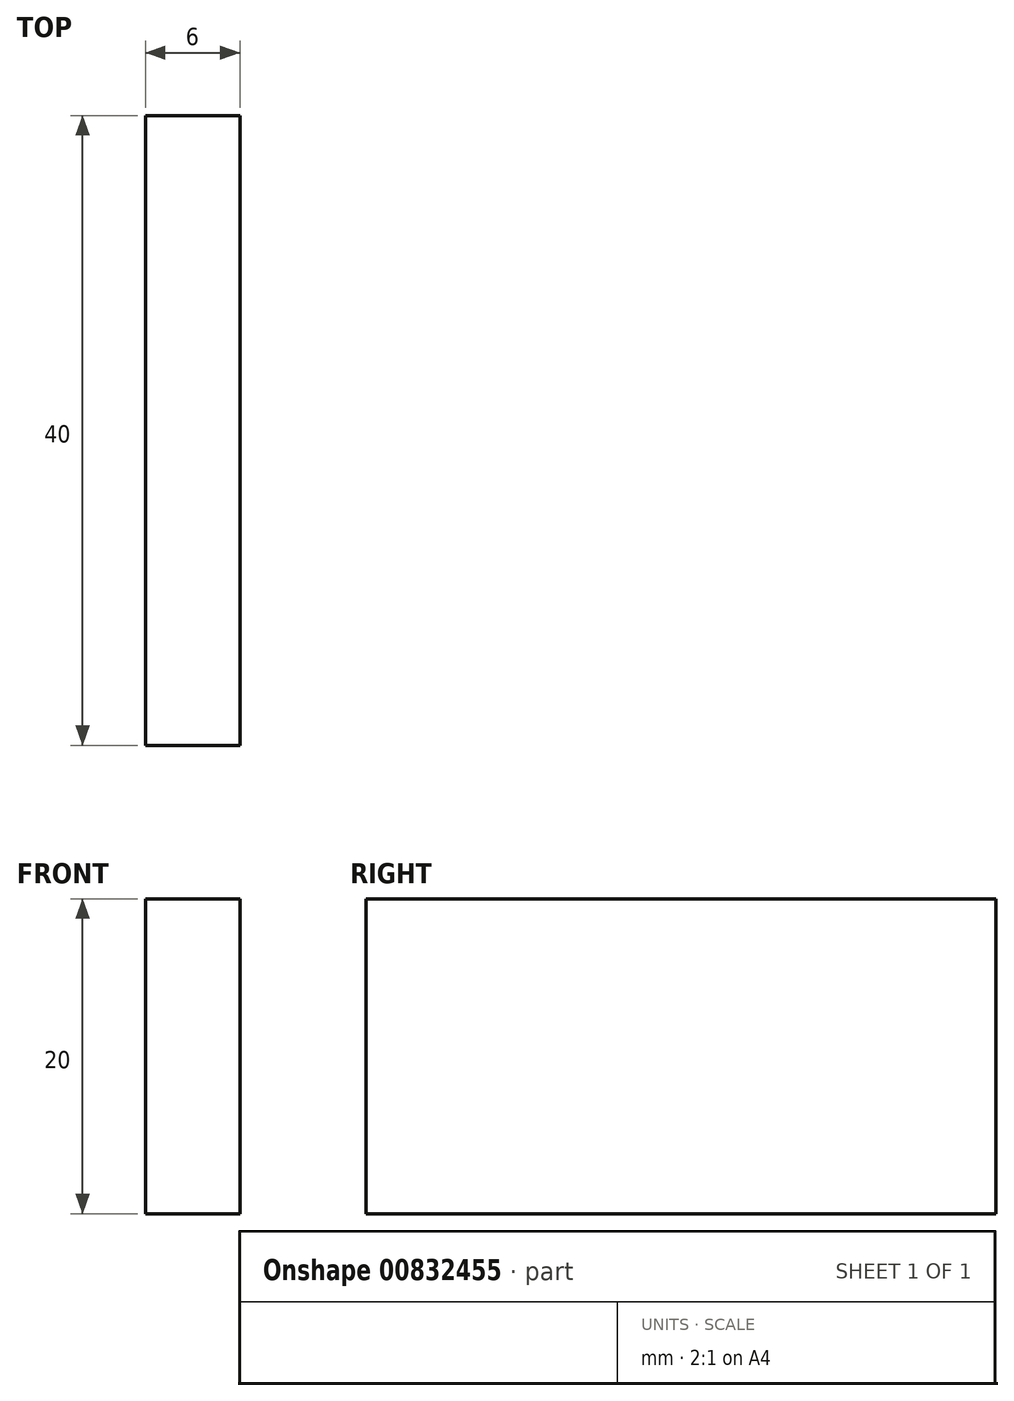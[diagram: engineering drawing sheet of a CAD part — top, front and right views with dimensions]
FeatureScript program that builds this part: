
annotation { "Feature Type Name" : "Feature", "Feature Type Description" : "" }
export const myFeature = defineFeature(function(context is Context, id is Id, definition is map)
    precondition{}
    {
        {
            var Q0;
            Q0=qCreatedBy(makeId("Right.planeOp"),FACE);
            var sketch = newSketch(context, id + "F0", { "sketchPlane" : qUnion([Q0])});
            skLineSegment(sketch, "E0.bottom", {"start": v(20, 10) * mm, "end": v(-20, 10) * mm});
            skLineSegment(sketch, "E0.top", {"start": v(20, -10) * mm, "end": v(-20, -10) * mm});
            skLineSegment(sketch, "E0.left", {"start": v(20, 10) * mm, "end": v(20, -10) * mm});
            skLineSegment(sketch, "E0.right", {"start": v(-20, 10) * mm, "end": v(-20, -10) * mm});
            skPoint(sketch, "E0.middle", {"position": v(0, 0) * mm});
            skSolve(sketch);
        }
        {
            var Q0;
            Q0=makeQuery(id+"F0.imprint","IMPRINT",FACE,{"disambiguationData":[TD([[makeQuery(id+"F0.imprint","IMPRINT",EDGE,{"derivedFrom":sQuery(id+"F0.wireOp",EDGE,"E0.bottom")}),1.0]])]});
            extrude(context, id + "F1", {"entities" : qUnion([Q0]), "depth" : 6 * mm, "offsetDistance" : 25 * mm});
        }
    });
